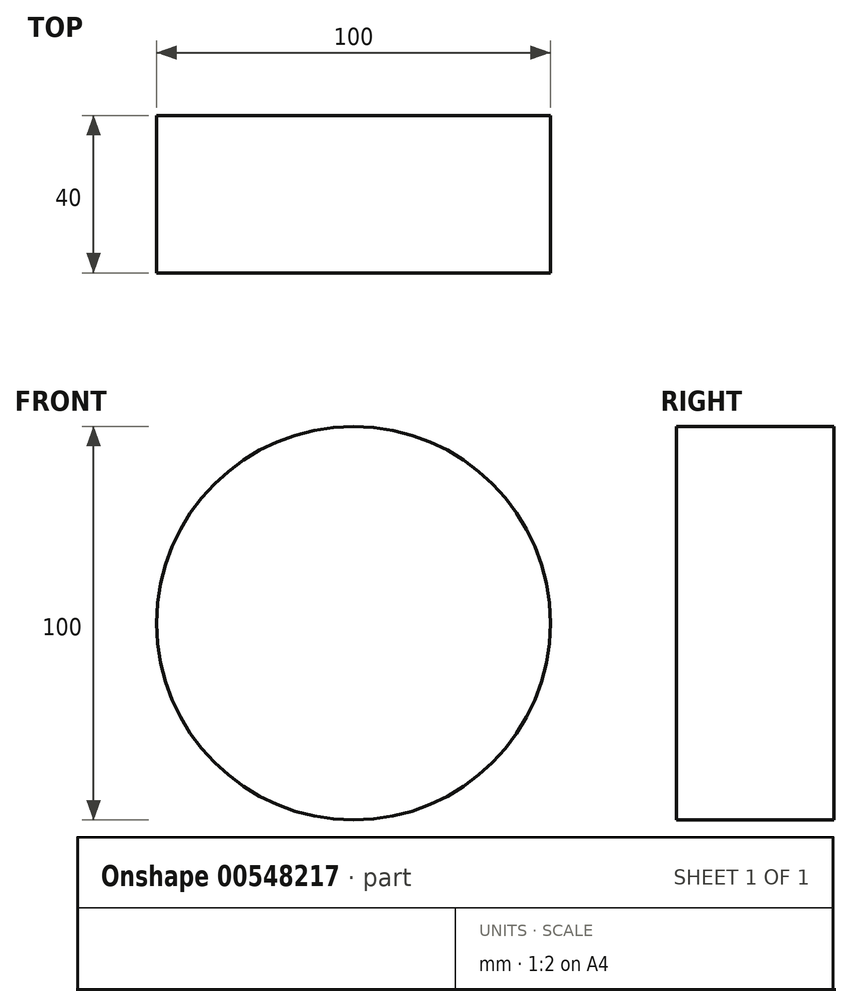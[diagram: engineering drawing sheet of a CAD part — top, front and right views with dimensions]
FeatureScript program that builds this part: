
annotation { "Feature Type Name" : "Feature", "Feature Type Description" : "" }
export const myFeature = defineFeature(function(context is Context, id is Id, definition is map)
    precondition{}
    {
        {
            var Q0;
            Q0=qCreatedBy(makeId("Front.planeOp"),FACE);
            var sketch = newSketch(context, id + "F0", { "sketchPlane" : qUnion([Q0])});
            skCircle(sketch, "E0", {"center": v(0, 0) * mm, "radius": 50 * mm});
            skSolve(sketch);
        }
        {
            var Q0;
            Q0 = qSketchRegion(id + "F0", true);
            extrude(context, id + "F1", {"entities" : qUnion([Q0]), "depth" : 40 * mm, "offsetDistance" : 25 * mm});
        }
    });
